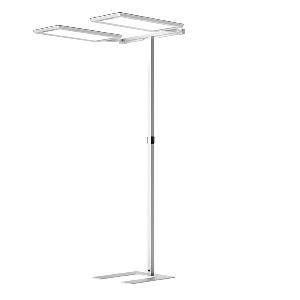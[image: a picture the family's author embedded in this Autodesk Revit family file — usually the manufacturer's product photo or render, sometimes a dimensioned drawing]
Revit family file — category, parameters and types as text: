
# Revit family: yara_doubleu_-_yus_2_8000_840_r_sr_cee_00_c_114268000-00815001_cad4
name_source: partatom
category: Lighting Fixtures
units: mm (PartAtom-declared; Revit-internal decimal feet)

## family parameters
Cut with Voids When Loaded = No
Host = Face
Light Source = No
Part Type = Normal
Room Calculation Point = No
Round Connector Dimension = Use Diameter
Shared = No

## types (1)
- YARA.doubleU - YUS 2/8000/840/R/SR/CEE/00/C (1 x LED, 8000 lm, 4000K)
    Apparent Load = 112 VA
    Approval mark = CE
    CIE Flux Codes = 58 87 97 13 100
    Color Rendering = 80-89
    Color Temperature = 4000K
    Control Gear = Electronic ballast
    Default Elevation = 1800 mm
    Description = YUS 2/8000/840/R/SR/CEE/00/C|Free-standing luminaire|light source: LED Cold white   |work equipment: Electronic ballast DALI|power factor: approx. 0,966|luminous flux: 16000 lm|light distribution: Direct/indirect|direct ratio: approx. 13 %|color rendering index (CRI): >= 80|chromaticity tolerance:  3 SDCM|technology: Presence and daylight sensor control (PIR)|operation: Wireless switch|luminaire body|material: Aluminium/plastic|surface: Powder coatet|colour: Silver metallic|lamp cover: Acrylic (PMMA)|tubular section|material: Steel tube|surface: Powder-coated|Form: Tubular section upright|colour of tubular section: Silver metallic|luminaire base|Form: C-form flat|weight (net): approx. 26.0 kg|mains lead: 3.00 m Mains plug CEE 7/VII|Fastening: Floor standing base|glare control: Conical prismatic screen|unified glare rating(4H 8H): <=  16|special features: App control, Asymmetric radiation, Direct and indirect lighting component with edge light and light guidetechnology for a homogeneous light exit, Flicker-free, Magnetic control panel, freely positionable, PIR movement and daylight sensor, TALK Bluetooth|Approval mark: VDE - ENEC|
    Frequency = 50 Hz, 60 Hz
    Height = 24 mm  [stored 0.0787402 ft]
    Lamp = 1 x LED
    Lamp Light Flux = 8000 lm
    Lamp count = 1
    Length = 690 mm
    Luminous efficacy = 143 lm/W
    Manufacturer = Waldmann
    ModVariant = No
    Model = 114268000-00815001
    Mounting Place = Floor
    Mounting Type = Freestanding
    Number of Poles = 1
    OnlyDefault = Yes
    Power Factor = 1
    Product Name = YARA.doubleU - YUS 2/8000/840/R/SR/CEE/00/C
    Product group = Free standing luminaire
    ProductGroupID = 13
    Protection Class = Protection class I
    Protection Degree = IP 20
    RLX_Detail_Level = 1
    RlxData = <blob elided: 68913 chars, md5=b560f448>
    Socket = socket
    Standby Power = 0 W
    System Light Flux = 16000 lm
    System Power = 112 W
    Type Comments = Product without accessories
    Type Image = yus-r-sr-c.jpg
    URL = http://relux.com
    VarID = ---
    Voltage = 230 V
    Voltage Range = 220-240 V
    Weight = 0.00 kg
    Width = 358 mm

note: [stored X ft] marks values corroborated as IEEE doubles in the binary element streams (Revit-internal decimal feet)

## geometry (parser evidence)
native form markers: Blend x4, Sweep x18
no freeform markers — native parametric forms only
